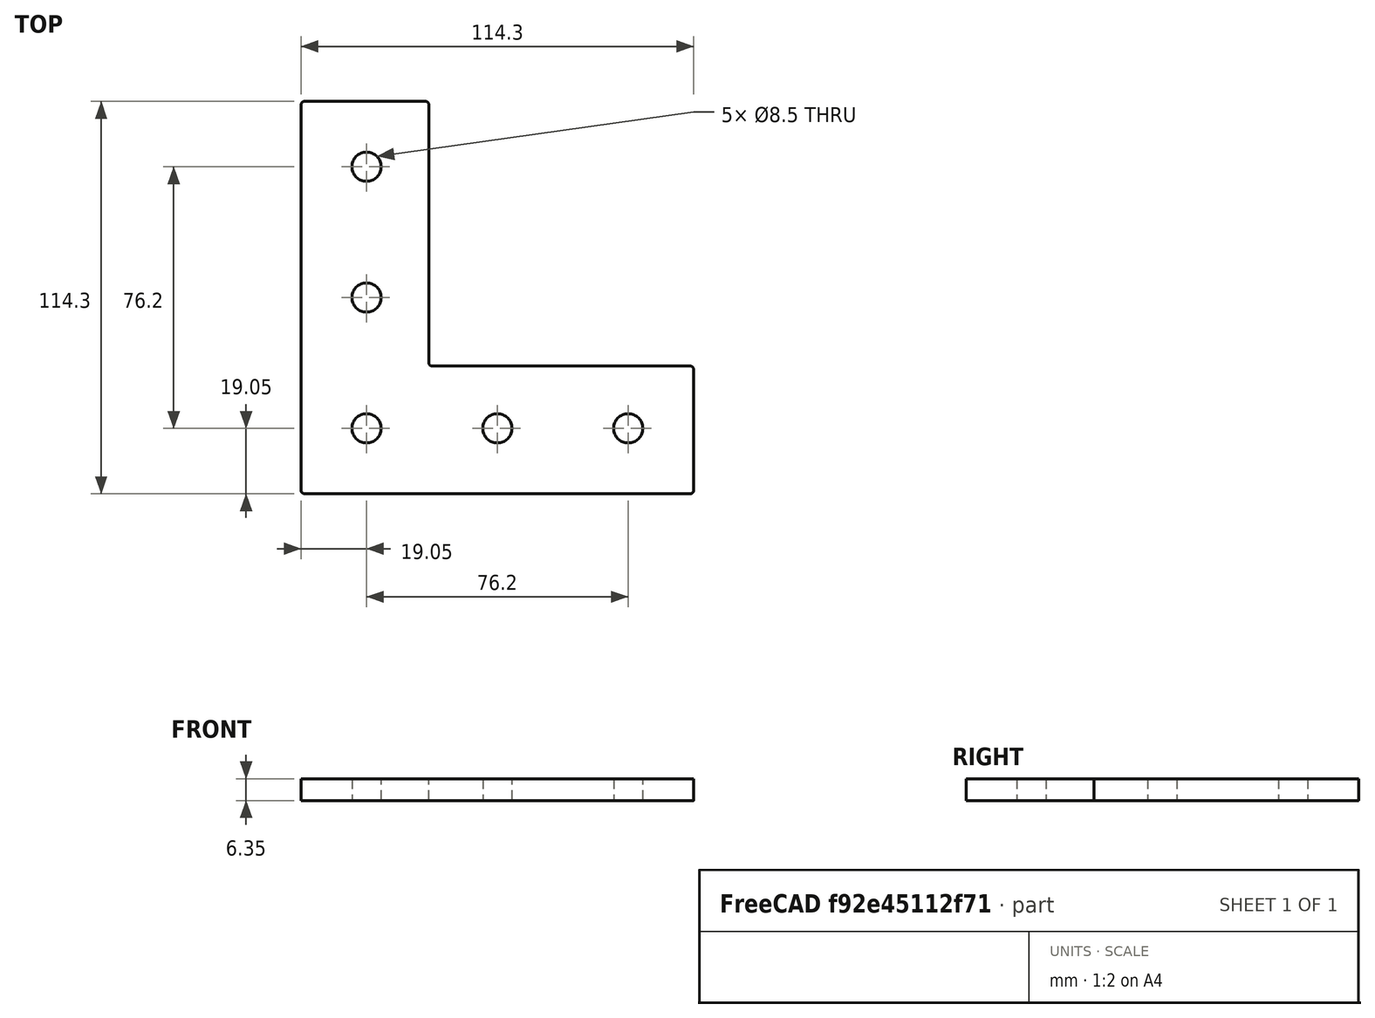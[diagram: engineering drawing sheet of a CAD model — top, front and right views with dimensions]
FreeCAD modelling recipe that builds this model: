
FCSTD DOCUMENT  (FreeCAD 0.18R)
Label: 1515-corner-plate
License: All rights reserved
LicenseURL: http://en.wikipedia.org/wiki/All_rights_reserved
objects: Sketcher::SketchObject×1, PartDesign::Pad×1, PartDesign::Body×1
note: 4 computed .brp shape members not serialized (recipe doc carries the construction recipe); baked Part::Feature solids carry a one-line shape summary decoded from their .brp

FEATURE [Sketcher::SketchObject] Sketch
  MapMode = 5
  Support = -> [XY_Plane]
  sketch-geometry (17):
    g0: LineSegment StartX=-113.3 StartY=114.3 StartZ=0 EndX=-78.1144 EndY=114.3 EndZ=0
    g1: LineSegment StartX=-77.1144 StartY=113.3 StartZ=0 EndX=-77.1144 EndY=38.1856 EndZ=0
    g2: LineSegment StartX=-76.1144 StartY=37.1856 StartZ=0 EndX=-1 EndY=37.1856 EndZ=0
    g3: LineSegment StartX=-8.7e-15 StartY=36.1856 StartZ=0 EndX=0 EndY=1 EndZ=0
    g4: LineSegment StartX=-1 StartY=0 StartZ=0 EndX=-113.3 EndY=0 EndZ=0
    g5: LineSegment StartX=-114.3 StartY=113.3 StartZ=0 EndX=-114.3 EndY=1 EndZ=0
    g6: ArcOfCircle CenterX=-113.3 CenterY=113.3 CenterZ=0 NormalX=0 NormalY=0 NormalZ=1 AngleXU=0 Radius=1 StartAngle=1.5708 EndAngle=3.14159
    g7: ArcOfCircle CenterX=-78.1144 CenterY=113.3 CenterZ=0 NormalX=0 NormalY=0 NormalZ=1 AngleXU=0 Radius=1 StartAngle=4.4e-15 EndAngle=1.5708
    g8: ArcOfCircle CenterX=-76.1144 CenterY=38.1856 CenterZ=0 NormalX=0 NormalY=0 NormalZ=1 AngleXU=0 Radius=1 StartAngle=3.14159 EndAngle=4.71239
    g9: ArcOfCircle CenterX=-1 CenterY=36.1856 CenterZ=0 NormalX=0 NormalY=0 NormalZ=1 AngleXU=0 Radius=1 StartAngle=-2.7e-15 EndAngle=1.5708
    g10: ArcOfCircle CenterX=-1 CenterY=1 CenterZ=0 NormalX=0 NormalY=0 NormalZ=1 AngleXU=0 Radius=1 StartAngle=4.71239 EndAngle=6.28319
    g11: ArcOfCircle CenterX=-113.3 CenterY=1 CenterZ=0 NormalX=0 NormalY=0 NormalZ=1 AngleXU=0 Radius=1 StartAngle=3.14159 EndAngle=4.71239
    g12: Circle CenterX=-19.05 CenterY=19.05 CenterZ=0 NormalX=0 NormalY=0 NormalZ=1 AngleXU=0 Radius=4.25
    g13: Circle CenterX=-57.15 CenterY=19.05 CenterZ=0 NormalX=0 NormalY=0 NormalZ=1 AngleXU=0 Radius=4.25
    g14: Circle CenterX=-95.25 CenterY=19.05 CenterZ=0 NormalX=0 NormalY=0 NormalZ=1 AngleXU=0 Radius=4.25
    g15: Circle CenterX=-95.25 CenterY=57.15 CenterZ=0 NormalX=0 NormalY=0 NormalZ=1 AngleXU=0 Radius=4.25
    g16: Circle CenterX=-95.25 CenterY=95.25 CenterZ=0 NormalX=0 NormalY=0 NormalZ=1 AngleXU=0 Radius=4.25
  constraints (45):
    c: Horizontal(g0)
    c: Vertical(g1)
    c: Horizontal(g2)
    c: Vertical(g5)
    c: Tangent(g5,g6) = -1.5708
    c: Tangent(g0,g6) = 1.5708
    c: Tangent(g0,g7) = 1.5708
    c: Tangent(g1,g7) = 1.5708
    c: DistanceY(g-1,g0) = 114.3
    c: DistanceX(g1,g-1) = 77.1144
    c: DistanceY(g1,g0) = 1
    c: DistanceY(g5,g1) = 0
    c: Tangent(g1,g8) = -1.5708
    c: Tangent(g2,g8) = -1.5708
    c: Tangent(g2,g9) = 1.5708
    c: Tangent(g3,g9) = 1.5708
    c: Tangent(g3,g10) = 1.5708
    c: Tangent(g4,g10) = 1.5708
    c: Tangent(g5,g11) = -1.5708
    c: Tangent(g4,g11) = 1.5708
    c: DistanceY(g4,g5) = 1
    c: Horizontal(g4)
    c: DistanceX(g3,g-1) = 0
    c: DistanceY(g4,g-1) = 0
    c: DistanceY(g3,g2) = 1
    c: DistanceY(g2,g1) = 1
    c: DistanceY(g4,g3) = 1
    c: DistanceX(g4,g-1) = 1
    c: DistanceY(g-1,g2) = 37.1856
    c: Diameter(g12) = 8.5
    c: DistanceY(g-1,g12) = 19.05
    c: DistanceX(g12,g-1) = 19.05
    c: Equal(g13,g12)
    c: DistanceX(g13,g12) = 38.1
    c: DistanceY(g12,g13) = 0
    c: Equal(g14,g12)
    c: Equal(g15,g12)
    c: Equal(g16,g12)
    c: DistanceX(g15,g14) = 0
    c: DistanceX(g16,g14) = 0
    c: DistanceY(g15,g16) = 38.1
    c: DistanceY(g14,g15) = 38.1
    c: DistanceY(g13,g14) = 0
    c: DistanceX(g5,g1) = 37.1856
    c: DistanceX(g14,g13) = 38.1
FEATURE [PartDesign::Pad] Pad
  Length = 6.35
  Length2 = 100
  Profile = -> Sketch
  Type = 0
FEATURE [PartDesign::Body] Body  label="1515-corner-plate"
  Group = -> [Sketch,Pad]
  Origin = -> Origin
  Tip = -> Pad
